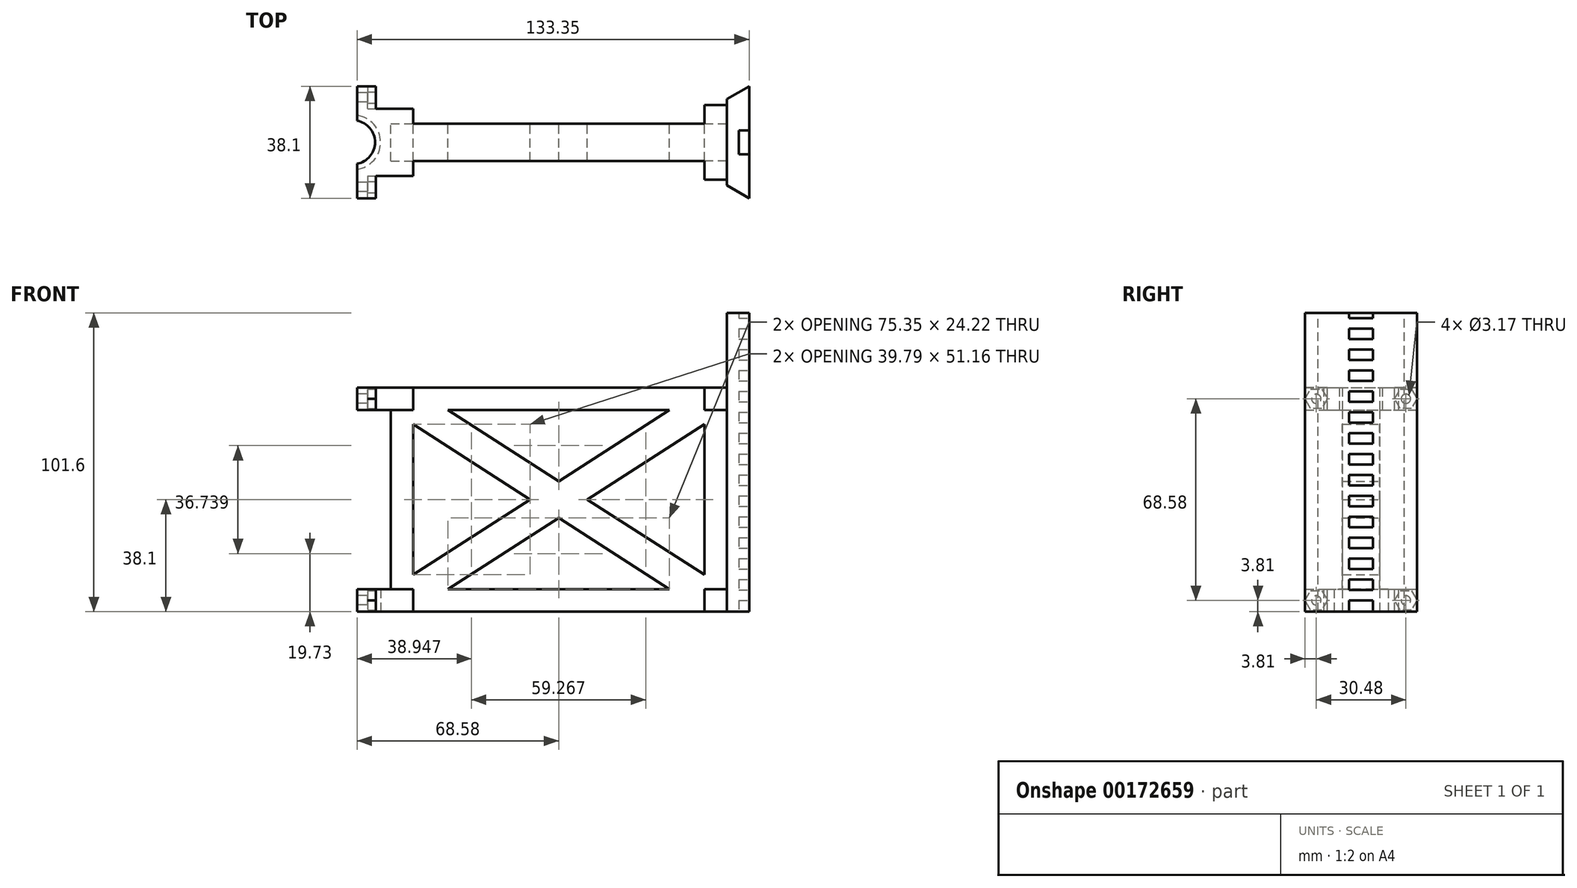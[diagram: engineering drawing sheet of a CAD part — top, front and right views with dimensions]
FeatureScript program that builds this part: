
annotation { "Feature Type Name" : "Feature", "Feature Type Description" : "" }
export const myFeature = defineFeature(function(context is Context, id is Id, definition is map)
    precondition{}
    {
        {
            var Q0;
            Q0=qCreatedBy(makeId("Front.planeOp"),FACE);
            var sketch = newSketch(context, id + "F0", { "sketchPlane" : qUnion([Q0])});
            skLineSegment(sketch, "E0", {"start": v(-57.15, 38.1) * mm, "end": v(57.15, 38.1) * mm});
            skLineSegment(sketch, "E1", {"start": v(-57.15, -38.1) * mm, "end": v(57.15, -38.1) * mm});
            skLineSegment(sketch, "E2", {"start": v(57.15, 38.1) * mm, "end": v(57.15, -38.1) * mm});
            skLineSegment(sketch, "E3", {"start": v(-57.15, 38.1) * mm, "end": v(-57.15, -38.1) * mm});
            skLineSegment(sketch, "E4", {"start": v(-57.15, 30.48) * mm, "end": v(57.15, 30.48) * mm});
            skLineSegment(sketch, "E5", {"start": v(57.15, -30.48) * mm, "end": v(-57.15, -30.48) * mm});
            skLineSegment(sketch, "E6", {"start": v(-49.53, 38.1) * mm, "end": v(-49.53, -38.1) * mm});
            skLineSegment(sketch, "E7", {"start": v(49.53, 38.1) * mm, "end": v(49.53, -38.1) * mm});
            skLineSegment(sketch, "E8", {"start": v(-57.15, 30.48) * mm, "end": v(49.53, -38.1) * mm});
            skLineSegment(sketch, "E9", {"start": v(57.15, -30.48) * mm, "end": v(-49.53, 38.1) * mm});
            skLineSegment(sketch, "E10", {"start": v(-49.53, -38.1) * mm, "end": v(57.15, 30.48) * mm});
            skLineSegment(sketch, "E11", {"start": v(49.53, 38.1) * mm, "end": v(-57.15, -30.48) * mm});
            skLineSegment(sketch, "E12", {"start": v(-57.15, -38.1) * mm, "end": v(-68.58, -38.1) * mm});
            skLineSegment(sketch, "E13", {"start": v(-57.15, -30.48) * mm, "end": v(-68.58, -30.48) * mm});
            skLineSegment(sketch, "E14", {"start": v(-57.15, 38.1) * mm, "end": v(-68.58, 38.1) * mm});
            skLineSegment(sketch, "E15", {"start": v(-57.15, 30.48) * mm, "end": v(-68.58, 30.48) * mm});
            skLineSegment(sketch, "E16", {"start": v(-68.58, 38.1) * mm, "end": v(-68.58, 30.48) * mm});
            skLineSegment(sketch, "E17", {"start": v(-68.58, -30.48) * mm, "end": v(-68.58, -38.1) * mm});
            skLineSegment(sketch, "E18", {"start": v(57.15, -38.1) * mm, "end": v(64.77, -38.1) * mm});
            skLineSegment(sketch, "E19", {"start": v(64.77, -38.1) * mm, "end": v(64.77, 63.5) * mm});
            skLineSegment(sketch, "E20", {"start": v(64.77, 63.5) * mm, "end": v(57.15, 63.5) * mm});
            skLineSegment(sketch, "E21", {"start": v(57.15, 63.5) * mm, "end": v(57.15, 38.1) * mm});
            skSolve(sketch);
        }
        {
            var Q0;
            {var subQ0=sQuery(id+"F0.wireOp",EDGE,"E9");var subQ5=sQuery(id+"F0.wireOp",EDGE,"E4");var subQ6=makeQuery(id+"F0.imprint","INTERSECT",VERTEX,{"derivedFrom":[subQ5,subQ0]});Q0=makeQuery(id+"F0.imprint","IMPRINT",FACE,{"disambiguationData":[TD([[makeQuery(id+"F0.imprint","IMPRINT",EDGE,{"disambiguationData":[TD([[subQ6,-1.0]])],"derivedFrom":subQ5}),1.0]])]});}
            var Q1;
            {var subQ3=sQuery(id+"F0.wireOp",EDGE,"E8");var subQ5=sQuery(id+"F0.wireOp",EDGE,"E5");var subQ6=makeQuery(id+"F0.imprint","INTERSECT",VERTEX,{"derivedFrom":[subQ5,subQ3]});Q1=makeQuery(id+"F0.imprint","IMPRINT",FACE,{"disambiguationData":[TD([[makeQuery(id+"F0.imprint","IMPRINT",EDGE,{"disambiguationData":[TD([[subQ6,-1.0]])],"derivedFrom":subQ5}),1.0]])]});}
            var Q2;
            {var subQ0=sQuery(id+"F0.wireOp",EDGE,"E8");var subQ5=sQuery(id+"F0.wireOp",EDGE,"E6");var subQ6=makeQuery(id+"F0.imprint","INTERSECT",VERTEX,{"derivedFrom":[subQ5,subQ0]});Q2=makeQuery(id+"F0.imprint","IMPRINT",FACE,{"disambiguationData":[TD([[makeQuery(id+"F0.imprint","IMPRINT",EDGE,{"disambiguationData":[TD([[subQ6,-1.0]])],"derivedFrom":subQ5}),-1.0]])]});}
            var Q3;
            {var subQ1=sQuery(id+"F0.wireOp",EDGE,"E4");var subQ3=sQuery(id+"F0.wireOp",EDGE,"E6");var subQ4=makeQuery(id+"F0.imprint","INTERSECT",VERTEX,{"derivedFrom":[subQ1,subQ3]});Q3=makeQuery(id+"F0.imprint","IMPRINT",FACE,{"disambiguationData":[TD([[makeQuery(id+"F0.imprint","IMPRINT",EDGE,{"disambiguationData":[TD([[subQ4,-1.0]])],"derivedFrom":subQ3}),-1.0]])]});}
            var Q4;
            {var subQ0=sQuery(id+"F0.wireOp",EDGE,"E6");var subQ1=sQuery(id+"F0.wireOp",EDGE,"E4");var subQ2=makeQuery(id+"F0.imprint","INTERSECT",VERTEX,{"derivedFrom":[subQ1,subQ0]});Q4=makeQuery(id+"F0.imprint","IMPRINT",FACE,{"disambiguationData":[TD([[makeQuery(id+"F0.imprint","IMPRINT",EDGE,{"disambiguationData":[TD([[subQ2,-1.0]])],"derivedFrom":subQ1}),1.0]])]});}
            var Q5;
            {var subQ0=sQuery(id+"F0.wireOp",EDGE,"E11");var subQ1=sQuery(id+"F0.wireOp",EDGE,"E4");var subQ2=makeQuery(id+"F0.imprint","INTERSECT",VERTEX,{"derivedFrom":[subQ1,subQ0]});Q5=makeQuery(id+"F0.imprint","IMPRINT",FACE,{"disambiguationData":[TD([[makeQuery(id+"F0.imprint","IMPRINT",EDGE,{"disambiguationData":[TD([[subQ2,-1.0]])],"derivedFrom":subQ1}),1.0]])]});}
            var Q6;
            {var subQ0=sQuery(id+"F0.wireOp",EDGE,"E7");var subQ1=sQuery(id+"F0.wireOp",EDGE,"E5");var subQ2=makeQuery(id+"F0.imprint","INTERSECT",VERTEX,{"derivedFrom":[subQ1,subQ0]});Q6=makeQuery(id+"F0.imprint","IMPRINT",FACE,{"disambiguationData":[TD([[makeQuery(id+"F0.imprint","IMPRINT",EDGE,{"disambiguationData":[TD([[subQ2,-1.0]])],"derivedFrom":subQ1}),1.0]])]});}
            var Q7;
            {var subQ0=sQuery(id+"F0.wireOp",EDGE,"E10");var subQ1=sQuery(id+"F0.wireOp",EDGE,"E5");var subQ2=makeQuery(id+"F0.imprint","INTERSECT",VERTEX,{"derivedFrom":[subQ1,subQ0]});Q7=makeQuery(id+"F0.imprint","IMPRINT",FACE,{"disambiguationData":[TD([[makeQuery(id+"F0.imprint","IMPRINT",EDGE,{"disambiguationData":[TD([[subQ2,-1.0]])],"derivedFrom":subQ1}),1.0]])]});}
            var Q8;
            {var subQ1=sQuery(id+"F0.wireOp",EDGE,"E5");var subQ3=sQuery(id+"F0.wireOp",EDGE,"E6");var subQ4=makeQuery(id+"F0.imprint","INTERSECT",VERTEX,{"derivedFrom":[subQ1,subQ3]});Q8=makeQuery(id+"F0.imprint","IMPRINT",FACE,{"disambiguationData":[TD([[makeQuery(id+"F0.imprint","IMPRINT",EDGE,{"disambiguationData":[TD([[subQ4,1.0]])],"derivedFrom":subQ3}),-1.0]])]});}
            var Q9;
            {var subQ0=sQuery(id+"F0.wireOp",EDGE,"E10");var subQ5=sQuery(id+"F0.wireOp",EDGE,"E7");var subQ7=makeQuery(id+"F0.imprint","INTERSECT",VERTEX,{"derivedFrom":[subQ5,subQ0]});Q9=makeQuery(id+"F0.imprint","IMPRINT",FACE,{"disambiguationData":[TD([[makeQuery(id+"F0.imprint","IMPRINT",EDGE,{"disambiguationData":[TD([[subQ7,-1.0]])],"derivedFrom":subQ5}),1.0]])]});}
            var Q10;
            {var subQ1=sQuery(id+"F0.wireOp",EDGE,"E5");var subQ3=sQuery(id+"F0.wireOp",EDGE,"E7");var subQ4=makeQuery(id+"F0.imprint","INTERSECT",VERTEX,{"derivedFrom":[subQ1,subQ3]});Q10=makeQuery(id+"F0.imprint","IMPRINT",FACE,{"disambiguationData":[TD([[makeQuery(id+"F0.imprint","IMPRINT",EDGE,{"disambiguationData":[TD([[subQ4,1.0]])],"derivedFrom":subQ3}),1.0]])]});}
            var Q11;
            {var subQ1=sQuery(id+"F0.wireOp",EDGE,"E4");var subQ3=sQuery(id+"F0.wireOp",EDGE,"E7");var subQ4=makeQuery(id+"F0.imprint","INTERSECT",VERTEX,{"derivedFrom":[subQ1,subQ3]});Q11=makeQuery(id+"F0.imprint","IMPRINT",FACE,{"disambiguationData":[TD([[makeQuery(id+"F0.imprint","IMPRINT",EDGE,{"disambiguationData":[TD([[subQ4,-1.0]])],"derivedFrom":subQ3}),1.0]])]});}
            var Q12;
            {var subQ3=sQuery(id+"F0.wireOp",EDGE,"E11");var subQ7=sQuery(id+"F0.wireOp",EDGE,"E4");var subQ9=makeQuery(id+"F0.imprint","INTERSECT",VERTEX,{"derivedFrom":[subQ7,subQ3]});Q12=makeQuery(id+"F0.imprint","IMPRINT",FACE,{"disambiguationData":[TD([[makeQuery(id+"F0.imprint","IMPRINT",EDGE,{"disambiguationData":[TD([[subQ9,-1.0]])],"derivedFrom":subQ7}),-1.0]])]});}
            var Q13;
            {var subQ1=sQuery(id+"F0.wireOp",EDGE,"E5");var subQ5=sQuery(id+"F0.wireOp",EDGE,"E7");var subQ6=makeQuery(id+"F0.imprint","INTERSECT",VERTEX,{"derivedFrom":[subQ1,subQ5]});Q13=makeQuery(id+"F0.imprint","IMPRINT",FACE,{"disambiguationData":[TD([[makeQuery(id+"F0.imprint","IMPRINT",EDGE,{"disambiguationData":[TD([[subQ6,-1.0]])],"derivedFrom":subQ1}),-1.0]])]});}
            var Q14;
            {var subQ0=sQuery(id+"F0.wireOp",EDGE,"E10");var subQ1=sQuery(id+"F0.wireOp",EDGE,"E5");var subQ2=makeQuery(id+"F0.imprint","INTERSECT",VERTEX,{"derivedFrom":[subQ1,subQ0]});Q14=makeQuery(id+"F0.imprint","IMPRINT",FACE,{"disambiguationData":[TD([[makeQuery(id+"F0.imprint","IMPRINT",EDGE,{"disambiguationData":[TD([[subQ2,-1.0]])],"derivedFrom":subQ1}),-1.0]])]});}
            var Q15;
            {var subQ1=sQuery(id+"F0.wireOp",EDGE,"E4");var subQ6=sQuery(id+"F0.wireOp",EDGE,"E6");var subQ9=makeQuery(id+"F0.imprint","INTERSECT",VERTEX,{"derivedFrom":[subQ1,subQ6]});Q15=makeQuery(id+"F0.imprint","IMPRINT",FACE,{"disambiguationData":[TD([[makeQuery(id+"F0.imprint","IMPRINT",EDGE,{"disambiguationData":[TD([[subQ9,-1.0]])],"derivedFrom":subQ1}),-1.0]])]});}
            var Q16;
            {var subQ0=sQuery(id+"F0.wireOp",EDGE,"E11");var subQ1=sQuery(id+"F0.wireOp",EDGE,"E8");var subQ2=makeQuery(id+"F0.imprint","INTERSECT",VERTEX,{"derivedFrom":[subQ1,subQ0]});Q16=makeQuery(id+"F0.imprint","IMPRINT",FACE,{"disambiguationData":[TD([[makeQuery(id+"F0.imprint","IMPRINT",EDGE,{"disambiguationData":[TD([[subQ2,-1.0]])],"derivedFrom":subQ1}),1.0]])]});}
            extrude(context, id + "F1", {"entities" : qUnion([Q0, Q1, Q2, Q3, Q4, Q5, Q6, Q7, Q8, Q9, Q10, Q11, Q12, Q13, Q14, Q15, Q16]), "endBound" : BoundingType.SYMMETRIC, "depth" : 12.7 * mm});
        }
        {
            var Q0;
            {var subQ0=sQuery(id+"F0.wireOp",EDGE,"E17");Q0=makeQuery(id+"F0.imprint","IMPRINT",FACE,{"disambiguationData":[TD([[makeQuery(id+"F0.imprint","IMPRINT",EDGE,{"derivedFrom":subQ0}),1.0]])]});}
            var Q1;
            {var subQ5=sQuery(id+"F0.wireOp",EDGE,"ElOXMjrr-WFoR-BwOV-4qWE-z5U341Nr3btm");Q1=makeQuery(id+"F0.imprint","IMPRINT",FACE,{"disambiguationData":[TD([[makeQuery(id+"F0.imprint","IMPRINT",EDGE,{"derivedFrom":subQ5}),1.0]])]});}
            var Q2;
            {var subQ0=sQuery(id+"F0.wireOp",EDGE,"E14");Q2=makeQuery(id+"F0.imprint","IMPRINT",FACE,{"disambiguationData":[TD([[makeQuery(id+"F0.imprint","IMPRINT",EDGE,{"derivedFrom":subQ0}),1.0]])]});}
            var Q3;
            {var subQ3=sQuery(id+"F0.wireOp",EDGE,"E6");var subQ5=sQuery(id+"F0.wireOp",EDGE,"E5");var subQ7=makeQuery(id+"F0.imprint","INTERSECT",VERTEX,{"derivedFrom":[subQ5,subQ3]});Q3=makeQuery(id+"F0.imprint","IMPRINT",FACE,{"disambiguationData":[TD([[makeQuery(id+"F0.imprint","IMPRINT",EDGE,{"disambiguationData":[TD([[subQ7,-1.0]])],"derivedFrom":subQ3}),-1.0]])]});}
            var Q4;
            {var subQ3=sQuery(id+"F0.wireOp",EDGE,"E6");var subQ5=sQuery(id+"F0.wireOp",EDGE,"E4");var subQ7=makeQuery(id+"F0.imprint","INTERSECT",VERTEX,{"derivedFrom":[subQ5,subQ3]});Q4=makeQuery(id+"F0.imprint","IMPRINT",FACE,{"disambiguationData":[TD([[makeQuery(id+"F0.imprint","IMPRINT",EDGE,{"disambiguationData":[TD([[subQ7,1.0]])],"derivedFrom":subQ3}),-1.0]])]});}
            extrude(context, id + "F2", {"entities" : qUnion([Q0, Q1, Q2, Q3, Q4]), "operationType" : NewBodyOperationType.ADD, "endBound" : BoundingType.SYMMETRIC, "depth" : 38.1 * mm});
        }
        {
            var Q0;
            {var subQ0=sQuery(id+"F0.wireOp",EDGE,"E18");Q0=makeQuery(id+"F0.imprint","IMPRINT",FACE,{"disambiguationData":[TD([[makeQuery(id+"F0.imprint","IMPRINT",EDGE,{"derivedFrom":subQ0}),1.0]])]});}
            extrude(context, id + "F3", {"entities" : qUnion([Q0]), "operationType" : NewBodyOperationType.ADD, "endBound" : BoundingType.SYMMETRIC, "depth" : 38.1 * mm});
        }
        {
            var Q0;
            {var subQ3=sQuery(id+"F0.wireOp",EDGE,"E7");var subQ5=sQuery(id+"F0.wireOp",EDGE,"E4");var subQ7=makeQuery(id+"F0.imprint","INTERSECT",VERTEX,{"derivedFrom":[subQ5,subQ3]});Q0=makeQuery(id+"F0.imprint","IMPRINT",FACE,{"disambiguationData":[TD([[makeQuery(id+"F0.imprint","IMPRINT",EDGE,{"disambiguationData":[TD([[subQ7,-1.0]])],"derivedFrom":subQ5}),1.0]])]});}
            var Q1;
            {var subQ3=sQuery(id+"F0.wireOp",EDGE,"E7");var subQ5=sQuery(id+"F0.wireOp",EDGE,"E5");var subQ7=makeQuery(id+"F0.imprint","INTERSECT",VERTEX,{"derivedFrom":[subQ5,subQ3]});Q1=makeQuery(id+"F0.imprint","IMPRINT",FACE,{"disambiguationData":[TD([[makeQuery(id+"F0.imprint","IMPRINT",EDGE,{"disambiguationData":[TD([[subQ7,1.0]])],"derivedFrom":subQ5}),1.0]])]});}
            extrude(context, id + "F4", {"entities" : qUnion([Q0, Q1]), "operationType" : NewBodyOperationType.ADD, "endBound" : BoundingType.SYMMETRIC, "depth" : 25.4 * mm});
        }
        {
            var Q0;
            Q0=makeQuery(id+"F3.opExtrude","SWEPT_FACE",FACE,{"disambiguationData":[OSD([sQuery(id+"F0.wireOp",EDGE,"E20")])]});
            var sketch = newSketch(context, id + "F5", { "sketchPlane" : qUnion([Q0])});
            skLineSegment(sketch, "E22", {"start": v(64.77, -19.05) * mm, "end": v(57.15, -14.65) * mm});
            skLineSegment(sketch, "E23", {"start": v(64.77, 19.05) * mm, "end": v(57.15, 14.65) * mm});
            skSolve(sketch);
        }
        {
            var Q0;
            {var subQ0=sQuery(id+"F5.wireOp",EDGE,"E23");Q0=makeQuery(id+"F5.imprint","IMPRINT",FACE,{"disambiguationData":[TD([[makeQuery(id+"F5.imprint","IMPRINT",EDGE,{"derivedFrom":subQ0}),-1.0]])]});}
            var Q1;
            {var subQ0=sQuery(id+"F5.wireOp",EDGE,"E22");Q1=makeQuery(id+"F5.imprint","IMPRINT",FACE,{"disambiguationData":[TD([[makeQuery(id+"F5.imprint","IMPRINT",EDGE,{"derivedFrom":subQ0}),1.0]])]});}
            extrude(context, id + "F6", {"entities" : qUnion([Q0, Q1]), "operationType" : NewBodyOperationType.REMOVE, "oppositeDirection" : true, "depth" : 127 * mm});
        }
        {
            var Q0;
            {var subQ0=sQuery(id+"F0.wireOp",EDGE,"E1");Q0=makeQuery(id+"F3.boolean.opBoolean","MERGE",FACE,{"derivedFrom":[makeQuery(id+"F2.boolean.opBoolean","MERGE",FACE,{"derivedFrom":[makeQuery(id+"F1.opExtrude","SWEPT_FACE",FACE,{"disambiguationData":[OSD([subQ0])]}),makeQuery(id+"F2.opExtrude","SWEPT_FACE",FACE,{"disambiguationData":[OSD([subQ0,sQuery(id+"F0.wireOp",EDGE,"E12")])]}),makeQuery(id+"F2.opExtrude","SWEPT_FACE",FACE,{"disambiguationData":[OSD([subQ0])]})]}),makeQuery(id+"F3.opExtrude","SWEPT_FACE",FACE,{"disambiguationData":[OSD([sQuery(id+"F0.wireOp",EDGE,"E18")])]})]});}
            var sketch = newSketch(context, id + "F7", { "sketchPlane" : qUnion([Q0])});
            skLineSegment(sketch, "E24", {"start": v(-57.15, 19.05) * mm, "end": v(-57.15, -19.05) * mm, "construction": true});
            skCircle(sketch, "E25", {"center": v(-69.85, 0) * mm, "radius": 12.7 * mm});
            skCircle(sketch, "E26", {"center": v(-69.85, 0) * mm, "radius": 9.14 * mm});
            skLineSegment(sketch, "E27", {"start": v(-69.85, 19.05) * mm, "end": v(-69.85, -19.05) * mm});
            skLineSegment(sketch, "E28", {"start": v(-68.58, 19.05) * mm, "end": v(-68.58, -19.05) * mm});
            skLineSegment(sketch, "E29", {"start": v(-71.12, 19.05) * mm, "end": v(-71.12, -19.05) * mm});
            skSolve(sketch);
        }
        {
            var Q0;
            Q0=sQuery(id+"F7.wireOp",VERTEX,"E26.center");
            var Q1;
            Q1=makeQuery(id+"F1.opExtrude","SWEPT_BODY",BODY,{"disambiguationData":[OSD([sQuery(id+"F0.wireOp",EDGE,"E0"),sQuery(id+"F0.wireOp",EDGE,"E1"),sQuery(id+"F0.wireOp",EDGE,"E2"),sQuery(id+"F0.wireOp",EDGE,"E3"),sQuery(id+"F0.wireOp",EDGE,"E4"),sQuery(id+"F0.wireOp",EDGE,"E5"),sQuery(id+"F0.wireOp",EDGE,"E6"),sQuery(id+"F0.wireOp",EDGE,"E7"),sQuery(id+"F0.wireOp",EDGE,"E8"),sQuery(id+"F0.wireOp",EDGE,"E9"),sQuery(id+"F0.wireOp",EDGE,"E10"),sQuery(id+"F0.wireOp",EDGE,"E11")])]});
            hole(context, id + "F8", {"style" : HoleStyle.SIMPLE, "endStyle" : HoleEndStyle.BLIND, "holeDiameter" : 18.54 * mm, "holeDepth" : 7.62 * mm, "startFromSketch" : true, "locations" : qUnion([Q0]), "scope" : qUnion([Q1])});
        }
        {
            var Q0;
            {var subQ0=sQuery(id+"F0.wireOp",EDGE,"E0");Q0=makeQuery(id+"F2.boolean.opBoolean","MERGE",FACE,{"derivedFrom":[makeQuery(id+"F1.opExtrude","SWEPT_FACE",FACE,{"disambiguationData":[OSD([subQ0])]}),makeQuery(id+"F2.opExtrude","SWEPT_FACE",FACE,{"disambiguationData":[OSD([subQ0,sQuery(id+"F0.wireOp",EDGE,"E14")])]}),makeQuery(id+"F2.opExtrude","SWEPT_FACE",FACE,{"disambiguationData":[OSD([subQ0])]})]});}
            var sketch = newSketch(context, id + "F9", { "sketchPlane" : qUnion([Q0])});
            skLineSegment(sketch, "E30", {"start": v(-57.15, 19.05) * mm, "end": v(-57.15, -19.05) * mm, "construction": true});
            skCircle(sketch, "E31", {"center": v(-69.85, 0) * mm, "radius": 12.7 * mm});
            skCircle(sketch, "E32", {"center": v(-69.85, 0) * mm, "radius": 6.99 * mm});
            skLineSegment(sketch, "E33", {"start": v(-68.58, -11.43) * mm, "end": v(-49.53, -11.43) * mm});
            skLineSegment(sketch, "E34", {"start": v(-68.58, 11.43) * mm, "end": v(-49.53, 11.43) * mm});
            skLineSegment(sketch, "E35", {"start": v(-69.85, -19.05) * mm, "end": v(-69.85, 19.05) * mm, "construction": true});
            skLineSegment(sketch, "E36", {"start": v(-62.23, 19.05) * mm, "end": v(-62.23, 11.43) * mm});
            skLineSegment(sketch, "E37", {"start": v(-77.47, 19.05) * mm, "end": v(-77.47, 11.43) * mm});
            skLineSegment(sketch, "E38.trimOffspring", {"start": v(-62.23, -11.43) * mm, "end": v(-62.23, -19.05) * mm});
            skLineSegment(sketch, "E39.trimOffspring", {"start": v(-77.47, -11.43) * mm, "end": v(-77.47, -19.05) * mm});
            skSolve(sketch);
        }
        {
            var Q0;
            Q0=sQuery(id+"F9.wireOp",VERTEX,"E32.center");
            var Q1;
            Q1=makeQuery(id+"F1.opExtrude","SWEPT_BODY",BODY,{"disambiguationData":[OSD([sQuery(id+"F0.wireOp",EDGE,"E0"),sQuery(id+"F0.wireOp",EDGE,"E1"),sQuery(id+"F0.wireOp",EDGE,"E2"),sQuery(id+"F0.wireOp",EDGE,"E3"),sQuery(id+"F0.wireOp",EDGE,"E4"),sQuery(id+"F0.wireOp",EDGE,"E5"),sQuery(id+"F0.wireOp",EDGE,"E6"),sQuery(id+"F0.wireOp",EDGE,"E7"),sQuery(id+"F0.wireOp",EDGE,"E8"),sQuery(id+"F0.wireOp",EDGE,"E9"),sQuery(id+"F0.wireOp",EDGE,"E10"),sQuery(id+"F0.wireOp",EDGE,"E11")])]});
            hole(context, id + "F10", {"style" : HoleStyle.SIMPLE, "endStyle" : HoleEndStyle.BLIND, "holeDiameter" : 14.83 * mm, "holeDepth" : 7.62 * mm, "startFromSketch" : true, "locations" : qUnion([Q0]), "scope" : qUnion([Q1])});
        }
        {
            var Q0;
            Q0=makeQuery(id+"F3.opExtrude","SWEPT_FACE",FACE,{"disambiguationData":[OSD([sQuery(id+"F0.wireOp",EDGE,"E19")])]});
            var sketch = newSketch(context, id + "F11", { "sketchPlane" : qUnion([Q0])});
            skLineSegment(sketch, "E40", {"start": v(4.06, 63.5) * mm, "end": v(4.06, -38.1) * mm});
            skLineSegment(sketch, "E41", {"start": v(-4.06, 63.5) * mm, "end": v(-4.06, -38.1) * mm});
            skLineSegment(sketch, "E42", {"start": v(0, 63.5) * mm, "end": v(0, -38.1) * mm, "construction": true});
            skLineSegment(sketch, "E43", {"start": v(-4.06, 61.72) * mm, "end": v(4.06, 61.72) * mm});
            skLineSegment(sketch, "E44", {"start": v(-4.06, 58.17) * mm, "end": v(4.06, 58.17) * mm});
            skLineSegment(sketch, "E45", {"start": v(-4.06, 54.61) * mm, "end": v(4.06, 54.61) * mm});
            skLineSegment(sketch, "E46", {"start": v(-4.06, 51.05) * mm, "end": v(4.06, 51.05) * mm});
            skLineSegment(sketch, "E47", {"start": v(-4.06, 47.5) * mm, "end": v(4.06, 47.5) * mm});
            skLineSegment(sketch, "E48", {"start": v(-4.06, 43.94) * mm, "end": v(4.06, 43.94) * mm});
            skLineSegment(sketch, "E49", {"start": v(-4.06, 40.39) * mm, "end": v(4.06, 40.39) * mm});
            skLineSegment(sketch, "E50", {"start": v(-4.06, 36.83) * mm, "end": v(4.06, 36.83) * mm});
            skLineSegment(sketch, "E51", {"start": v(-4.06, 33.27) * mm, "end": v(4.06, 33.27) * mm});
            skLineSegment(sketch, "E52", {"start": v(-4.06, 29.72) * mm, "end": v(4.06, 29.72) * mm});
            skLineSegment(sketch, "E53", {"start": v(4.06, 26.16) * mm, "end": v(-4.06, 26.16) * mm});
            skLineSegment(sketch, "E54", {"start": v(-4.06, 22.6) * mm, "end": v(4.06, 22.6) * mm});
            skLineSegment(sketch, "E55", {"start": v(-4.06, 19.05) * mm, "end": v(4.06, 19.05) * mm});
            skLineSegment(sketch, "E56", {"start": v(-4.06, 15.5) * mm, "end": v(4.06, 15.5) * mm});
            skLineSegment(sketch, "E57", {"start": v(4.06, 11.94) * mm, "end": v(-4.06, 11.94) * mm});
            skLineSegment(sketch, "E58", {"start": v(-4.06, 8.38) * mm, "end": v(4.06, 8.38) * mm});
            skLineSegment(sketch, "E59", {"start": v(-4.06, 4.83) * mm, "end": v(4.06, 4.83) * mm});
            skLineSegment(sketch, "E60", {"start": v(-4.06, 1.27) * mm, "end": v(4.06, 1.27) * mm});
            skLineSegment(sketch, "E61", {"start": v(4.06, -2.29) * mm, "end": v(-4.06, -2.29) * mm});
            skLineSegment(sketch, "E62", {"start": v(-4.06, -5.84) * mm, "end": v(4.06, -5.84) * mm});
            skLineSegment(sketch, "E63", {"start": v(-4.06, -9.4) * mm, "end": v(4.06, -9.4) * mm});
            skLineSegment(sketch, "E64", {"start": v(4.06, -12.95) * mm, "end": v(-4.06, -12.95) * mm});
            skLineSegment(sketch, "E65", {"start": v(-4.06, -16.51) * mm, "end": v(4.06, -16.51) * mm});
            skLineSegment(sketch, "E66", {"start": v(4.06, -20.07) * mm, "end": v(-4.06, -20.07) * mm});
            skLineSegment(sketch, "E67", {"start": v(-4.06, -23.62) * mm, "end": v(4.06, -23.62) * mm});
            skLineSegment(sketch, "E68", {"start": v(4.06, -27.18) * mm, "end": v(-4.06, -27.18) * mm});
            skLineSegment(sketch, "E69", {"start": v(-4.06, -30.73) * mm, "end": v(4.06, -30.73) * mm});
            skLineSegment(sketch, "E70", {"start": v(-4.06, -34.3) * mm, "end": v(4.06, -34.3) * mm});
            skSolve(sketch);
        }
        {
            var Q0;
            {var subQ3=sQuery(id+"F11.wireOp",EDGE,"E43");Q0=makeQuery(id+"F11.imprint","IMPRINT",FACE,{"disambiguationData":[TD([[makeQuery(id+"F11.imprint","IMPRINT",EDGE,{"derivedFrom":subQ3}),1.0]])]});}
            var Q1;
            {var subQ0=sQuery(id+"F11.wireOp",EDGE,"E44");Q1=makeQuery(id+"F11.imprint","IMPRINT",FACE,{"disambiguationData":[TD([[makeQuery(id+"F11.imprint","IMPRINT",EDGE,{"derivedFrom":subQ0}),-1.0]])]});}
            var Q2;
            {var subQ0=sQuery(id+"F11.wireOp",EDGE,"E46");Q2=makeQuery(id+"F11.imprint","IMPRINT",FACE,{"disambiguationData":[TD([[makeQuery(id+"F11.imprint","IMPRINT",EDGE,{"derivedFrom":subQ0}),-1.0]])]});}
            var Q3;
            {var subQ0=sQuery(id+"F11.wireOp",EDGE,"E48");Q3=makeQuery(id+"F11.imprint","IMPRINT",FACE,{"disambiguationData":[TD([[makeQuery(id+"F11.imprint","IMPRINT",EDGE,{"derivedFrom":subQ0}),-1.0]])]});}
            var Q4;
            {var subQ0=sQuery(id+"F11.wireOp",EDGE,"E50");Q4=makeQuery(id+"F11.imprint","IMPRINT",FACE,{"disambiguationData":[TD([[makeQuery(id+"F11.imprint","IMPRINT",EDGE,{"derivedFrom":subQ0}),-1.0]])]});}
            var Q5;
            {var subQ0=sQuery(id+"F11.wireOp",EDGE,"E52");Q5=makeQuery(id+"F11.imprint","IMPRINT",FACE,{"disambiguationData":[TD([[makeQuery(id+"F11.imprint","IMPRINT",EDGE,{"derivedFrom":subQ0}),-1.0]])]});}
            var Q6;
            {var subQ0=sQuery(id+"F11.wireOp",EDGE,"E54");Q6=makeQuery(id+"F11.imprint","IMPRINT",FACE,{"disambiguationData":[TD([[makeQuery(id+"F11.imprint","IMPRINT",EDGE,{"derivedFrom":subQ0}),-1.0]])]});}
            var Q7;
            {var subQ0=sQuery(id+"F11.wireOp",EDGE,"E56");Q7=makeQuery(id+"F11.imprint","IMPRINT",FACE,{"disambiguationData":[TD([[makeQuery(id+"F11.imprint","IMPRINT",EDGE,{"derivedFrom":subQ0}),-1.0]])]});}
            var Q8;
            {var subQ0=sQuery(id+"F11.wireOp",EDGE,"E58");Q8=makeQuery(id+"F11.imprint","IMPRINT",FACE,{"disambiguationData":[TD([[makeQuery(id+"F11.imprint","IMPRINT",EDGE,{"derivedFrom":subQ0}),-1.0]])]});}
            var Q9;
            {var subQ0=sQuery(id+"F11.wireOp",EDGE,"E60");Q9=makeQuery(id+"F11.imprint","IMPRINT",FACE,{"disambiguationData":[TD([[makeQuery(id+"F11.imprint","IMPRINT",EDGE,{"derivedFrom":subQ0}),-1.0]])]});}
            var Q10;
            {var subQ3=sQuery(id+"F11.wireOp",EDGE,"E62");Q10=makeQuery(id+"F11.imprint","IMPRINT",FACE,{"disambiguationData":[TD([[makeQuery(id+"F11.imprint","IMPRINT",EDGE,{"derivedFrom":subQ3}),-1.0]])]});}
            var Q11;
            {var subQ0=sQuery(id+"F11.wireOp",EDGE,"E64");Q11=makeQuery(id+"F11.imprint","IMPRINT",FACE,{"disambiguationData":[TD([[makeQuery(id+"F11.imprint","IMPRINT",EDGE,{"derivedFrom":subQ0}),1.0]])]});}
            var Q12;
            {var subQ0=sQuery(id+"F11.wireOp",EDGE,"E66");Q12=makeQuery(id+"F11.imprint","IMPRINT",FACE,{"disambiguationData":[TD([[makeQuery(id+"F11.imprint","IMPRINT",EDGE,{"derivedFrom":subQ0}),1.0]])]});}
            var Q13;
            {var subQ0=sQuery(id+"F11.wireOp",EDGE,"E68");Q13=makeQuery(id+"F11.imprint","IMPRINT",FACE,{"disambiguationData":[TD([[makeQuery(id+"F11.imprint","IMPRINT",EDGE,{"derivedFrom":subQ0}),1.0]])]});}
            var Q14;
            {var subQ3=sQuery(id+"F11.wireOp",EDGE,"E70");Q14=makeQuery(id+"F11.imprint","IMPRINT",FACE,{"disambiguationData":[TD([[makeQuery(id+"F11.imprint","IMPRINT",EDGE,{"derivedFrom":subQ3}),-1.0]])]});}
            extrude(context, id + "F12", {"entities" : qUnion([Q0, Q1, Q2, Q3, Q4, Q5, Q6, Q7, Q8, Q9, Q10, Q11, Q12, Q13, Q14]), "operationType" : NewBodyOperationType.REMOVE, "oppositeDirection" : true, "depth" : 3.56 * mm});
        }
        {
            var Q0;
            Q0=makeQuery(id+"F2.opExtrude","SWEPT_FACE",FACE,{"disambiguationData":[OSD([sQuery(id+"F0.wireOp",EDGE,"E16")])]});
            var sketch = newSketch(context, id + "F13", { "sketchPlane" : qUnion([Q0])});
            skLineSegment(sketch, "E71", {"start": v(-19.05, 34.29) * mm, "end": v(19.05, 34.29) * mm, "construction": true});
            skCircle(sketch, "E72", {"center": v(-15.24, 34.29) * mm, "radius": 1.59 * mm});
            skCircle(sketch, "E73", {"center": v(15.24, 34.29) * mm, "radius": 1.59 * mm});
            skCircle(sketch, "E74", {"center": v(15.24, 34.29) * mm, "radius": 2.92 * mm});
            skCircle(sketch, "E75", {"center": v(-15.24, 34.29) * mm, "radius": 2.92 * mm});
            skSolve(sketch);
        }
        {
            var Q0;
            Q0=makeQuery(id+"F2.opExtrude","SWEPT_FACE",FACE,{"disambiguationData":[OSD([sQuery(id+"F0.wireOp",EDGE,"E17")])]});
            var sketch = newSketch(context, id + "F14", { "sketchPlane" : qUnion([Q0])});
            skLineSegment(sketch, "E76", {"start": v(-19.05, -34.3) * mm, "end": v(19.05, -34.3) * mm, "construction": true});
            skCircle(sketch, "E77", {"center": v(-15.24, -34.3) * mm, "radius": 1.59 * mm});
            skCircle(sketch, "E78", {"center": v(-15.24, -34.3) * mm, "radius": 2.92 * mm});
            skCircle(sketch, "E79", {"center": v(15.24, -34.3) * mm, "radius": 2.92 * mm});
            skCircle(sketch, "E80", {"center": v(15.24, -34.3) * mm, "radius": 1.59 * mm});
            skSolve(sketch);
        }
        {
            var Q0;
            {var subQ11=sQuery(id+"F9.wireOp",EDGE,"E36");Q0=makeQuery(id+"F9.imprint","IMPRINT",FACE,{"disambiguationData":[TD([[makeQuery(id+"F9.imprint","IMPRINT",EDGE,{"derivedFrom":subQ11}),1.0]])]});}
            var Q1;
            {var subQ4=sQuery(id+"F9.wireOp",EDGE,"E37");Q1=makeQuery(id+"F9.imprint","IMPRINT",FACE,{"disambiguationData":[TD([[makeQuery(id+"F9.imprint","IMPRINT",EDGE,{"derivedFrom":subQ4}),-1.0]])]});}
            var Q2;
            {var subQ4=sQuery(id+"F9.wireOp",EDGE,"E39.trimOffspring");Q2=makeQuery(id+"F9.imprint","IMPRINT",FACE,{"disambiguationData":[TD([[makeQuery(id+"F9.imprint","IMPRINT",EDGE,{"derivedFrom":subQ4}),-1.0]])]});}
            var Q3;
            {var subQ11=sQuery(id+"F9.wireOp",EDGE,"E38.trimOffspring");Q3=makeQuery(id+"F9.imprint","IMPRINT",FACE,{"disambiguationData":[TD([[makeQuery(id+"F9.imprint","IMPRINT",EDGE,{"derivedFrom":subQ11}),1.0]])]});}
            extrude(context, id + "F15", {"entities" : qUnion([Q0, Q1, Q2, Q3]), "operationType" : NewBodyOperationType.REMOVE, "endBound" : BoundingType.THROUGH_ALL, "oppositeDirection" : true, "depth" : 25.4 * mm});
        }
        {
            var Q0;
            Q0=makeQuery(id+"F13.imprint","IMPRINT",FACE,{"disambiguationData":[TD([[makeQuery(id+"F13.imprint","IMPRINT",EDGE,{"derivedFrom":sQuery(id+"F13.wireOp",EDGE,"E72")}),1.0]])]});
            var Q1;
            Q1=makeQuery(id+"F13.imprint","IMPRINT",FACE,{"disambiguationData":[TD([[makeQuery(id+"F13.imprint","IMPRINT",EDGE,{"derivedFrom":sQuery(id+"F13.wireOp",EDGE,"E73")}),1.0]])]});
            var Q2;
            Q2=makeQuery(id+"F14.imprint","IMPRINT",FACE,{"disambiguationData":[TD([[makeQuery(id+"F14.imprint","IMPRINT",EDGE,{"derivedFrom":sQuery(id+"F14.wireOp",EDGE,"E80")}),1.0]])]});
            var Q3;
            Q3=makeQuery(id+"F14.imprint","IMPRINT",FACE,{"disambiguationData":[TD([[makeQuery(id+"F14.imprint","IMPRINT",EDGE,{"derivedFrom":sQuery(id+"F14.wireOp",EDGE,"E77")}),1.0]])]});
            extrude(context, id + "F16", {"entities" : qUnion([Q0, Q1, Q2, Q3]), "operationType" : NewBodyOperationType.REMOVE, "oppositeDirection" : true, "depth" : 38.1 * mm});
        }
        {
            var Q0;
            {var subQ0=sQuery(id+"F0.wireOp",EDGE,"E0");var subQ9=makeQuery(id+"F1.opExtrude","SWEPT_FACE",FACE,{"disambiguationData":[OSD([subQ0])]});var subQ12=sQuery(id+"F9.wireOp",EDGE,"E36");Q0=makeQuery(id+"F15.boolean.opBoolean","COPY",FACE,{"disambiguationData":[TD([subQ9])],"derivedFrom":makeQuery(id+"F15.opExtrude","SWEPT_FACE",FACE,{"disambiguationData":[OSD([subQ12])]})});}
            var sketch = newSketch(context, id + "F17", { "sketchPlane" : qUnion([Q0])});
            skCircle(sketch, "E81.cCircle", {"center": v(15.24, 34.3) * mm, "radius": 3.3 * mm, "construction": true});
            skLineSegment(sketch, "E81.0", {"start": v(17.15, 37.6) * mm, "end": v(19.05, 34.29) * mm});
            skLineSegment(sketch, "E81.1", {"start": v(19.05, 34.3) * mm, "end": v(17.15, 30.99) * mm});
            skLineSegment(sketch, "E81.2", {"start": v(17.15, 30.99) * mm, "end": v(13.33, 30.99) * mm});
            skLineSegment(sketch, "E81.3", {"start": v(13.33, 30.99) * mm, "end": v(11.43, 34.3) * mm});
            skLineSegment(sketch, "E81.4", {"start": v(11.43, 34.29) * mm, "end": v(13.33, 37.6) * mm});
            skLineSegment(sketch, "E81.5", {"start": v(13.33, 37.6) * mm, "end": v(17.15, 37.6) * mm});
            skPoint(sketch, "E81.0.midPoint", {"position": v(18.1, 35.94) * mm});
            skSolve(sketch);
        }
        {
            var Q0;
            {var subQ0=sQuery(id+"F0.wireOp",EDGE,"E0");var subQ9=makeQuery(id+"F1.opExtrude","SWEPT_FACE",FACE,{"disambiguationData":[OSD([subQ0])]});var subQ12=sQuery(id+"F9.wireOp",EDGE,"E38.trimOffspring");Q0=makeQuery(id+"F15.boolean.opBoolean","COPY",FACE,{"disambiguationData":[TD([subQ9])],"derivedFrom":makeQuery(id+"F15.opExtrude","SWEPT_FACE",FACE,{"disambiguationData":[OSD([subQ12])]})});}
            var sketch = newSketch(context, id + "F18", { "sketchPlane" : qUnion([Q0])});
            skCircle(sketch, "E82.cCircle", {"center": v(-15.24, 34.3) * mm, "radius": 3.3 * mm, "construction": true});
            skLineSegment(sketch, "E82.0", {"start": v(-13.33, 37.6) * mm, "end": v(-11.43, 34.29) * mm});
            skLineSegment(sketch, "E82.1", {"start": v(-11.43, 34.3) * mm, "end": v(-13.33, 30.99) * mm});
            skLineSegment(sketch, "E82.2", {"start": v(-13.33, 30.99) * mm, "end": v(-17.15, 30.99) * mm});
            skLineSegment(sketch, "E82.3", {"start": v(-17.15, 30.99) * mm, "end": v(-19.05, 34.3) * mm});
            skLineSegment(sketch, "E82.4", {"start": v(-19.05, 34.3) * mm, "end": v(-17.15, 37.6) * mm});
            skLineSegment(sketch, "E82.5", {"start": v(-17.15, 37.6) * mm, "end": v(-13.33, 37.6) * mm});
            skPoint(sketch, "E82.0.midPoint", {"position": v(-12.38, 35.94) * mm});
            skSolve(sketch);
        }
        {
            var Q0;
            {var subQ0=sQuery(id+"F0.wireOp",EDGE,"E1");var subQ9=sQuery(id+"F9.wireOp",EDGE,"E36");Q0=makeQuery(id+"F15.boolean.opBoolean","COPY",FACE,{"disambiguationData":[TD([makeQuery(id+"F1.opExtrude","SWEPT_FACE",FACE,{"disambiguationData":[OSD([subQ0])]})])],"derivedFrom":makeQuery(id+"F15.opExtrude","SWEPT_FACE",FACE,{"disambiguationData":[OSD([subQ9])]})});}
            var sketch = newSketch(context, id + "F19", { "sketchPlane" : qUnion([Q0])});
            skCircle(sketch, "E83.cCircle", {"center": v(15.24, -34.3) * mm, "radius": 3.3 * mm, "construction": true});
            skLineSegment(sketch, "E83.0", {"start": v(17.15, -30.99) * mm, "end": v(19.05, -34.3) * mm});
            skLineSegment(sketch, "E83.1", {"start": v(19.05, -34.3) * mm, "end": v(17.15, -37.6) * mm});
            skLineSegment(sketch, "E83.2", {"start": v(17.15, -37.6) * mm, "end": v(13.33, -37.6) * mm});
            skLineSegment(sketch, "E83.3", {"start": v(13.33, -37.6) * mm, "end": v(11.43, -34.3) * mm});
            skLineSegment(sketch, "E83.4", {"start": v(11.43, -34.3) * mm, "end": v(13.33, -30.99) * mm});
            skLineSegment(sketch, "E83.5", {"start": v(13.33, -30.99) * mm, "end": v(17.15, -30.99) * mm});
            skPoint(sketch, "E83.0.midPoint", {"position": v(18.1, -32.64) * mm});
            skSolve(sketch);
        }
        {
            var Q0;
            {var subQ0=sQuery(id+"F0.wireOp",EDGE,"E1");var subQ7=sQuery(id+"F9.wireOp",EDGE,"E38.trimOffspring");Q0=makeQuery(id+"F15.boolean.opBoolean","COPY",FACE,{"disambiguationData":[TD([makeQuery(id+"F1.opExtrude","SWEPT_FACE",FACE,{"disambiguationData":[OSD([subQ0])]})])],"derivedFrom":makeQuery(id+"F15.opExtrude","SWEPT_FACE",FACE,{"disambiguationData":[OSD([subQ7])]})});}
            var sketch = newSketch(context, id + "F20", { "sketchPlane" : qUnion([Q0])});
            skCircle(sketch, "E84.cCircle", {"center": v(-15.24, -34.29) * mm, "radius": 3.3 * mm, "construction": true});
            skLineSegment(sketch, "E84.0", {"start": v(-13.33, -30.99) * mm, "end": v(-11.43, -34.29) * mm});
            skLineSegment(sketch, "E84.1", {"start": v(-11.43, -34.29) * mm, "end": v(-13.33, -37.6) * mm});
            skLineSegment(sketch, "E84.2", {"start": v(-13.33, -37.6) * mm, "end": v(-17.15, -37.6) * mm});
            skLineSegment(sketch, "E84.3", {"start": v(-17.15, -37.6) * mm, "end": v(-19.05, -34.3) * mm});
            skLineSegment(sketch, "E84.4", {"start": v(-19.05, -34.3) * mm, "end": v(-17.15, -30.99) * mm});
            skLineSegment(sketch, "E84.5", {"start": v(-17.15, -30.99) * mm, "end": v(-13.33, -30.99) * mm});
            skPoint(sketch, "E84.0.midPoint", {"position": v(-12.38, -32.64) * mm});
            skSolve(sketch);
        }
        {
            var Q0;
            Q0 = qSketchRegion(id + "F17", true);
            var Q1;
            {var subQ1=sQuery(id+"F18.wireOp",EDGE,"E82.2");Q1=makeQuery(id+"F18.imprint","IMPRINT",FACE,{"disambiguationData":[TD([[makeQuery(id+"F18.imprint","IMPRINT",EDGE,{"derivedFrom":subQ1}),-1.0]])]});}
            var Q2;
            {var subQ1=sQuery(id+"F20.wireOp",EDGE,"E84.2");Q2=makeQuery(id+"F20.imprint","IMPRINT",FACE,{"disambiguationData":[TD([[makeQuery(id+"F20.imprint","IMPRINT",EDGE,{"derivedFrom":subQ1}),-1.0]])]});}
            var Q3;
            {var subQ0=sQuery(id+"F19.wireOp",EDGE,"E83.2");Q3=makeQuery(id+"F19.imprint","IMPRINT",FACE,{"disambiguationData":[TD([[makeQuery(id+"F19.imprint","IMPRINT",EDGE,{"derivedFrom":subQ0}),-1.0]])]});}
            extrude(context, id + "F21", {"entities" : qUnion([Q0, Q1, Q2, Q3]), "operationType" : NewBodyOperationType.REMOVE, "oppositeDirection" : true, "depth" : 2.8 * mm});
        }
        {
            var Q0;
            Q0 = qSketchRegion(id + "F18", true);
            extrude(context, id + "F22", {"entities" : qUnion([Q0]), "operationType" : NewBodyOperationType.REMOVE, "oppositeDirection" : true, "depth" : 2.8 * mm});
        }
    });
